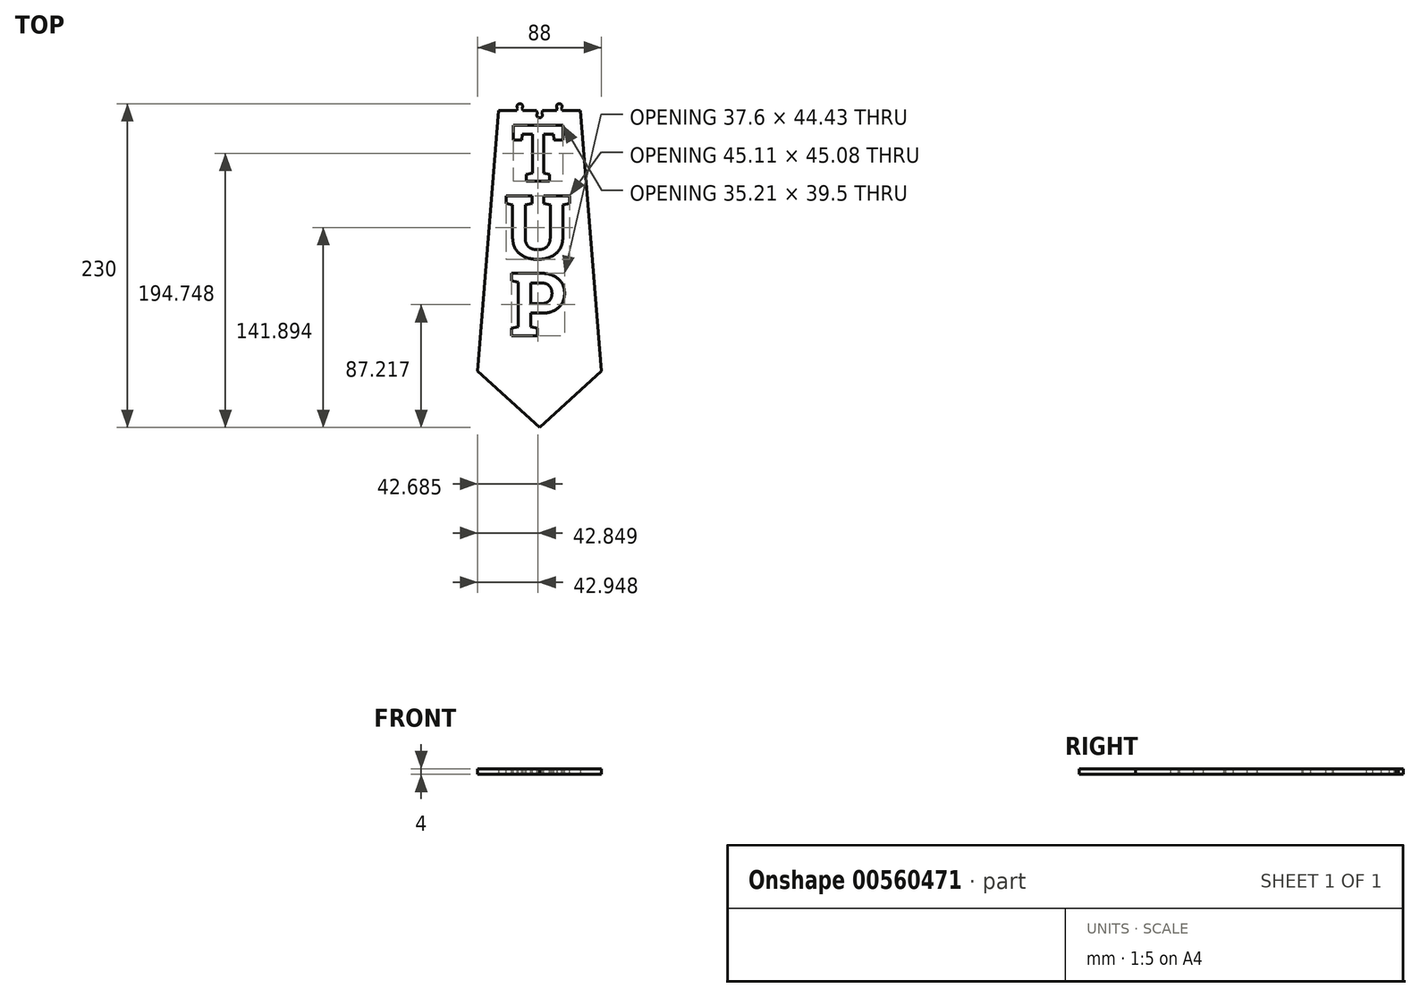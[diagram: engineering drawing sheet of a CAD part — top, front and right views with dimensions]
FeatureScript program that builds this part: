
annotation { "Feature Type Name" : "Feature", "Feature Type Description" : "" }
export const myFeature = defineFeature(function(context is Context, id is Id, definition is map)
    precondition{}
    {
        {
            var Q0;
            Q0=qCreatedBy(makeId("Top.planeOp"),FACE);
            var sketch = newSketch(context, id + "F0", { "sketchPlane" : qUnion([Q0])});
            skLineSegment(sketch, "E0", {"start": v(-1.09, 100.04) * mm, "end": v(-1.09, 94.88) * mm});
            skLineSegment(sketch, "E1", {"start": v(0.91, 100.04) * mm, "end": v(27.91, 100.04) * mm});
            skLineSegment(sketch, "E2", {"start": v(27.91, 100.04) * mm, "end": v(14.91, 100.04) * mm});
            skPoint(sketch, "E3", {"position": v(-15.09, 100.04) * mm});
            skPoint(sketch, "E4", {"position": v(-1.09, 100.04) * mm});
            skPoint(sketch, "E5", {"position": v(12.91, 100.04) * mm});
            skLineSegment(sketch, "E6", {"start": v(-17.09, 100.04) * mm, "end": v(-17.09, 101.04) * mm});
            skLineSegment(sketch, "E7", {"start": v(-13.09, 100.04) * mm, "end": v(-13.09, 101.04) * mm});
            skLineSegment(sketch, "E8", {"start": v(-3.09, 100.04) * mm, "end": v(-3.09, 99.04) * mm});
            skLineSegment(sketch, "E9", {"start": v(0.91, 100.04) * mm, "end": v(0.91, 98.88) * mm});
            skLineSegment(sketch, "E10", {"start": v(14.91, 100.04) * mm, "end": v(14.91, 101.04) * mm});
            skLineSegment(sketch, "E11", {"start": v(10.91, 100.04) * mm, "end": v(10.91, 101.04) * mm});
            skPoint(sketch, "E12", {"position": v(-1.09, 94.88) * mm});
            skArc(sketch, "E13", {"start": v(-2.42, 98.37) * mm, "mid": v(-1.14, 94.88) * mm, "end": v(0.33, 98.3) * mm});
            skLineSegment(sketch, "E14", {"start": v(-3.09, 99.04) * mm, "end": v(-2.42, 98.37) * mm});
            skPoint(sketch, "E15", {"position": v(12.91, 104.88) * mm});
            skArc(sketch, "E16", {"start": v(14.33, 101.63) * mm, "mid": v(12.91, 105.04) * mm, "end": v(11.5, 101.63) * mm});
            skLineSegment(sketch, "E17", {"start": v(10.91, 101.04) * mm, "end": v(11.5, 101.63) * mm});
            skArc(sketch, "E18", {"start": v(-13.67, 101.63) * mm, "mid": v(-15.09, 105.04) * mm, "end": v(-16.5, 101.63) * mm});
            skLineSegment(sketch, "E19", {"start": v(-13.09, 101.04) * mm, "end": v(-13.67, 101.63) * mm});
            skLineSegment(sketch, "E20", {"start": v(-17.09, 101.04) * mm, "end": v(-16.5, 101.63) * mm});
            skLineSegment(sketch, "E21.trimOffspring", {"start": v(-3.09, 100.04) * mm, "end": v(-13.09, 100.04) * mm});
            skLineSegment(sketch, "E22.trimOffspring", {"start": v(0.33, 98.3) * mm, "end": v(0.91, 98.88) * mm});
            skLineSegment(sketch, "E23.trimOffspring", {"start": v(14.33, 101.63) * mm, "end": v(14.91, 101.04) * mm});
            skLineSegment(sketch, "E24.trimOffspring", {"start": v(10.91, 100.04) * mm, "end": v(0.91, 100.04) * mm});
            skLineSegment(sketch, "E25.trimOffspring", {"start": v(-17.09, 100.04) * mm, "end": v(-30.09, 100.04) * mm});
            skPoint(sketch, "E26", {"position": v(-1.09, -84.96) * mm});
            skLineSegment(sketch, "E27", {"start": v(42.91, -84.96) * mm, "end": v(-1.09, -124.96) * mm});
            skLineSegment(sketch, "E28", {"start": v(-1.09, -124.96) * mm, "end": v(-45.09, -84.96) * mm});
            skLineSegment(sketch, "E29", {"start": v(-45.09, -84.96) * mm, "end": v(-30.09, 100.04) * mm});
            skLineSegment(sketch, "E30", {"start": v(27.91, 100.04) * mm, "end": v(42.91, -84.96) * mm});
            skSolve(sketch);
        }
        {
            var Q0;
            Q0=qSketchRegion(id+"F0",true);
            extrude(context, id + "F1", {"entities" : qUnion([Q0]), "depth" : 4 * mm, "offsetDistance" : 25 * mm});
        }
        {
            var Q0;
            Q0=makeQuery(id+"F1.opExtrude","CAP_FACE",FACE,{"disambiguationData":[OSD([sQuery(id+"F0.wireOp",EDGE,"E2"),sQuery(id+"F0.wireOp",EDGE,"E6"),sQuery(id+"F0.wireOp",EDGE,"E7"),sQuery(id+"F0.wireOp",EDGE,"E8"),sQuery(id+"F0.wireOp",EDGE,"E9"),sQuery(id+"F0.wireOp",EDGE,"E10"),sQuery(id+"F0.wireOp",EDGE,"E11"),sQuery(id+"F0.wireOp",EDGE,"E13"),sQuery(id+"F0.wireOp",EDGE,"E14"),sQuery(id+"F0.wireOp",EDGE,"E16"),sQuery(id+"F0.wireOp",EDGE,"E17"),sQuery(id+"F0.wireOp",EDGE,"E18"),sQuery(id+"F0.wireOp",EDGE,"E19"),sQuery(id+"F0.wireOp",EDGE,"E20"),sQuery(id+"F0.wireOp",EDGE,"E21.trimOffspring"),sQuery(id+"F0.wireOp",EDGE,"E22.trimOffspring"),sQuery(id+"F0.wireOp",EDGE,"E23.trimOffspring"),sQuery(id+"F0.wireOp",EDGE,"E24.trimOffspring"),sQuery(id+"F0.wireOp",EDGE,"E25.trimOffspring"),sQuery(id+"F0.wireOp",EDGE,"E27"),sQuery(id+"F0.wireOp",EDGE,"E28"),sQuery(id+"F0.wireOp",EDGE,"E29"),sQuery(id+"F0.wireOp",EDGE,"E30")])],"isStart":false});
            var sketch = newSketch(context, id + "F2", { "sketchPlane" : qUnion([Q0])});
            skLineSegment(sketch, "E31", {"start": v(-30.09, 100.04) * mm, "end": v(27.91, 100.04) * mm});
            skPoint(sketch, "E32", {"position": v(-1.09, 100.04) * mm});
            skLineSegment(sketch, "E33", {"start": v(-1.09, 100.04) * mm, "end": v(-1.09, -124.96) * mm});
            skLineSegment(sketch, "E34", {"start": v(-1.09, 90.04) * mm, "end": v(-30.9, 90.04) * mm});
            skLineSegment(sketch, "E35", {"start": v(-1.09, 90.04) * mm, "end": v(28.72, 90.04) * mm});
            skText(sketch, "E36", { "text": "T", "fontName": "RobotoSlab-Bold.ttf"});
            skText(sketch, "E37", { "text": "U", "fontName": "RobotoSlab-Bold.ttf"});
            skText(sketch, "E38", { "text": "P", "fontName": "RobotoSlab-Bold.ttf"});
            const initialGuessF2  = {"E36": [-0.02093, 0.05004, 1, 0, 0.04], "E37": [-0.02615, -0.00496, 1, 0, 0.045], "E38": [-0.02265, -0.05996, 1, 0, 0.045]};
            skSetInitialGuess(sketch, initialGuessF2);
            skSolve(sketch);
        }
        {
            var Q0;
            Q0 = qSketchRegion(id + "F2", true);
            extrude(context, id + "F3", {"entities" : qUnion([Q0]), "operationType" : NewBodyOperationType.REMOVE, "oppositeDirection" : true, "depth" : 4 * mm, "offsetDistance" : 25 * mm});
        }
    });
